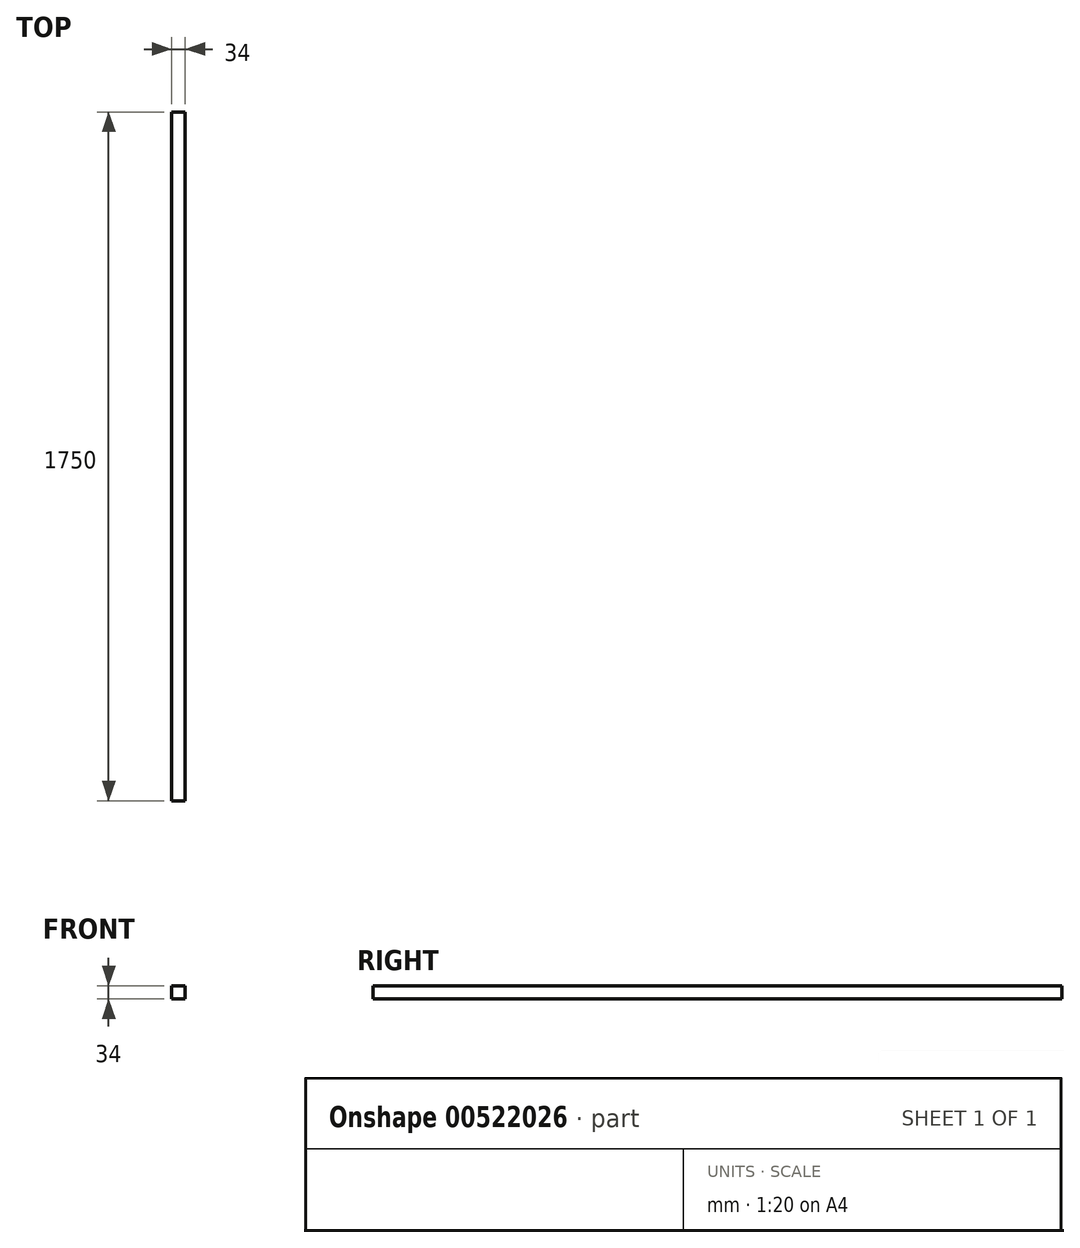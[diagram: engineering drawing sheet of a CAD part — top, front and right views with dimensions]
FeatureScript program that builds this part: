
annotation { "Feature Type Name" : "Feature", "Feature Type Description" : "" }
export const myFeature = defineFeature(function(context is Context, id is Id, definition is map)
    precondition{}
    {
        {
            var Q0;
            Q0=qCreatedBy(makeId("Top.planeOp"),FACE);
            var sketch = newSketch(context, id + "F0", { "sketchPlane" : qUnion([Q0])});
            skLineSegment(sketch, "E0.bottom", {"start": v(0, 0) * mm, "end": v(34, 0) * mm});
            skLineSegment(sketch, "E0.top", {"start": v(0, 1750) * mm, "end": v(34, 1750) * mm});
            skLineSegment(sketch, "E0.left", {"start": v(0, 0) * mm, "end": v(0, 1750) * mm});
            skLineSegment(sketch, "E0.right", {"start": v(34, 0) * mm, "end": v(34, 1750) * mm});
            skSolve(sketch);
        }
        {
            var Q0;
            Q0=makeQuery(id+"F0.imprint","IMPRINT",FACE,{"disambiguationData":[TD([[makeQuery(id+"F0.imprint","IMPRINT",EDGE,{"derivedFrom":sQuery(id+"F0.wireOp",EDGE,"E0.bottom")}),1.0]])]});
            extrude(context, id + "F1", {"entities" : qUnion([Q0]), "flatOperationType" : FlatOperationType.REMOVE, "depth" : 34 * mm, "offsetDistance" : 25 * mm, "domain" : OperationDomain.MODEL});
        }
    });
